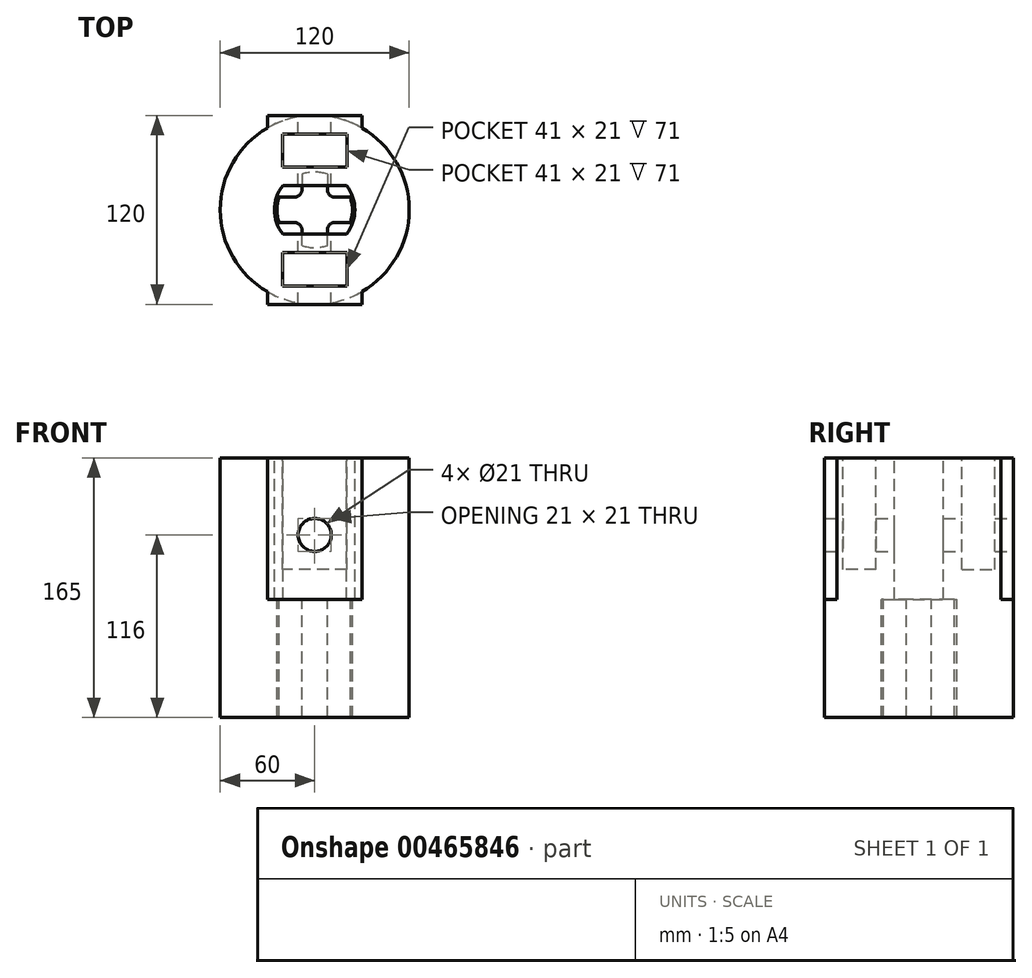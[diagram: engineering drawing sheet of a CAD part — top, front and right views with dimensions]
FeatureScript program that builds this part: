
annotation { "Feature Type Name" : "Feature", "Feature Type Description" : "" }
export const myFeature = defineFeature(function(context is Context, id is Id, definition is map)
    precondition{}
    {
        {
            var Q0;
            Q0=qCreatedBy(makeId("Top.planeOp"),FACE);
            var sketch = newSketch(context, id + "F0", { "sketchPlane" : qUnion([Q0])});
            skCircle(sketch, "E0", {"center": v(0, 0) * mm, "radius": 60 * mm});
            skLineSegment(sketch, "E1", {"start": v(-30, 51.96) * mm, "end": v(-30, 60) * mm});
            skLineSegment(sketch, "E2", {"start": v(-30, 60) * mm, "end": v(30, 60) * mm});
            skLineSegment(sketch, "E3", {"start": v(30, 60) * mm, "end": v(30, 51.96) * mm});
            skLineSegment(sketch, "E4", {"start": v(8, 22.63) * mm, "end": v(8, 13) * mm});
            skArc(sketch, "E5", {"start": v(8, 22.63) * mm, "mid": v(0, 24) * mm, "end": v(-8, 22.63) * mm});
            skArc(sketch, "E6", {"start": v(8, 13) * mm, "mid": v(9.46, 9.46) * mm, "end": v(13, 8) * mm});
            skLineSegment(sketch, "E7", {"start": v(-8, 22.63) * mm, "end": v(0, 0) * mm, "construction": true});
            skLineSegment(sketch, "E8", {"start": v(0, 0) * mm, "end": v(22.63, 8) * mm, "construction": true});
            skLineSegment(sketch, "E9", {"start": v(22.63, 8) * mm, "end": v(13, 8) * mm});
            skLineSegment(sketch, "E10", {"start": v(-8, 22.63) * mm, "end": v(8, 22.63) * mm, "construction": true});
            skArc(sketch, "E11.1.0", {"start": v(-22.63, 8) * mm, "mid": v(-24, 0) * mm, "end": v(-22.63, -8) * mm});
            skLineSegment(sketch, "E11.1.1", {"start": v(-22.63, 8) * mm, "end": v(-13, 8) * mm});
            skArc(sketch, "E11.1.2", {"start": v(-13, 8) * mm, "mid": v(-9.46, 9.46) * mm, "end": v(-8, 13) * mm});
            skLineSegment(sketch, "E11.1.3", {"start": v(-8, 22.63) * mm, "end": v(-8, 13) * mm});
            skArc(sketch, "E11.2.0", {"start": v(-8, -22.63) * mm, "mid": v(0, -24) * mm, "end": v(8, -22.63) * mm});
            skLineSegment(sketch, "E11.2.1", {"start": v(-8, -22.63) * mm, "end": v(-8, -13) * mm});
            skArc(sketch, "E11.2.2", {"start": v(-8, -13) * mm, "mid": v(-9.46, -9.46) * mm, "end": v(-13, -8) * mm});
            skLineSegment(sketch, "E11.2.3", {"start": v(-22.63, -8) * mm, "end": v(-13, -8) * mm});
            skArc(sketch, "E11.3.0", {"start": v(22.63, -8) * mm, "mid": v(24, 0) * mm, "end": v(22.63, 8) * mm});
            skLineSegment(sketch, "E11.3.1", {"start": v(22.63, -8) * mm, "end": v(13, -8) * mm});
            skArc(sketch, "E11.3.2", {"start": v(13, -8) * mm, "mid": v(9.46, -9.46) * mm, "end": v(8, -13) * mm});
            skLineSegment(sketch, "E11.3.3", {"start": v(8, -22.63) * mm, "end": v(8, -13) * mm});
            skLineSegment(sketch, "E12.1.0", {"start": v(-30, -60) * mm, "end": v(-30, -51.96) * mm});
            skLineSegment(sketch, "E12.1.1", {"start": v(30, -60) * mm, "end": v(-30, -60) * mm});
            skLineSegment(sketch, "E12.1.2", {"start": v(30, -51.96) * mm, "end": v(30, -60) * mm});
            skSolve(sketch);
        }
        {
            var Q0;
            Q0=qSketchRegion(id+"F0",true);
            var Q1;
            Q1=makeQuery(id+"F0.imprint","IMPRINT",FACE,{"disambiguationData":[TD([[makeQuery(id+"F0.imprint","IMPRINT",EDGE,{"derivedFrom":sQuery(id+"F0.wireOp",EDGE,"rkZdlgmY-ciTU-kQnJ-2yCQ-PcgXUmxzg4s6")}),-1.0]])]});
            var Q2;
            Q2=makeQuery(id+"F0.imprint","IMPRINT",FACE,{"disambiguationData":[TD([[makeQuery(id+"F0.imprint","IMPRINT",EDGE,{"derivedFrom":sQuery(id+"F0.wireOp",EDGE,"E4")}),-1.0]])]});
            extrude(context, id + "F1", {"entities" : qUnion([Q0, Q1, Q2]), "depth" : 90 * mm, "offsetDistance" : 25 * mm});
        }
        {
            var Q0;
            Q0=makeQuery(id+"F0.imprint","IMPRINT",FACE,{"disambiguationData":[TD([[makeQuery(id+"F0.imprint","IMPRINT",EDGE,{"derivedFrom":sQuery(id+"F0.wireOp",EDGE,"E4")}),1.0]])]});
            extrude(context, id + "F2", {"entities" : qUnion([Q0]), "operationType" : NewBodyOperationType.ADD, "oppositeDirection" : true, "depth" : 75 * mm, "offsetDistance" : 25 * mm});
        }
        {
            var Q0;
            Q0=makeQuery(id+"F1.opExtrude","CAP_FACE",FACE,{"disambiguationData":[OSD([sQuery(id+"F0.wireOp",EDGE,"E0")])],"isStart":false});
            var sketch = newSketch(context, id + "F3", { "sketchPlane" : qUnion([Q0])});
            skLineSegment(sketch, "E13", {"start": v(-20.25, 15.5) * mm, "end": v(20.25, -15.5) * mm, "construction": true});
            skPoint(sketch, "E14", {"position": v(0, 0) * mm});
            skPoint(sketch, "E15", {"position": v(0, 15.5) * mm});
            skCircle(sketch, "E16", {"center": v(0, 0) * mm, "radius": 25.5 * mm});
            skLineSegment(sketch, "E17", {"start": v(-20.25, -15.5) * mm, "end": v(20.25, -15.5) * mm});
            skLineSegment(sketch, "E18", {"start": v(-20.25, 15.5) * mm, "end": v(20.25, 15.5) * mm});
            skSolve(sketch);
        }
        {
            var Q0;
            {var subQ0=sQuery(id+"F3.wireOp",EDGE,"E16");var subQ1=sQuery(id+"F3.wireOp",EDGE,"5hhhO5J8-d6BO-3ee7-2W28-d0MtOCh9Vy86.bottom");var subQ2=makeQuery(id+"F3.imprint","INTERSECT",VERTEX,{"disambiguationData":[OD(0.0)],"derivedFrom":[subQ1,subQ0]});Q0=makeQuery(id+"F3.imprint","IMPRINT",FACE,{"disambiguationData":[TD([[makeQuery(id+"F3.imprint","IMPRINT",EDGE,{"disambiguationData":[TD([[subQ2,-1.0]])],"derivedFrom":subQ1}),-1.0]])]});}
            var Q1;
            {var subQ0=sQuery(id+"F3.wireOp",EDGE,"E17");Q1=makeQuery(id+"F3.imprint","IMPRINT",FACE,{"disambiguationData":[TD([[makeQuery(id+"F3.imprint","IMPRINT",EDGE,{"derivedFrom":subQ0}),1.0]])]});}
            extrude(context, id + "F4", {"entities" : qUnion([Q0, Q1]), "operationType" : NewBodyOperationType.REMOVE, "oppositeDirection" : true, "depth" : 90 * mm, "offsetDistance" : 25 * mm});
        }
        {
            var Q0;
            Q0=makeQuery(id+"F1.opExtrude","SWEPT_FACE",FACE,{"disambiguationData":[OSD([sQuery(id+"F0.wireOp",EDGE,"E2")])]});
            var sketch = newSketch(context, id + "F5", { "sketchPlane" : qUnion([Q0])});
            skSolve(sketch);
        }
        {
            var Q0;
            Q0=makeQuery(id+"F1.opExtrude","CAP_FACE",FACE,{"disambiguationData":[OSD([sQuery(id+"F0.wireOp",EDGE,"E0")])],"isStart":false});
            var sketch = newSketch(context, id + "F6", { "sketchPlane" : qUnion([Q0])});
            skLineSegment(sketch, "E19.bottom", {"start": v(-20.5, 27.25) * mm, "end": v(20.5, 27.25) * mm});
            skLineSegment(sketch, "E19.top", {"start": v(-20.5, 48.25) * mm, "end": v(20.5, 48.25) * mm});
            skLineSegment(sketch, "E19.left", {"start": v(-20.5, 27.25) * mm, "end": v(-20.5, 48.25) * mm});
            skLineSegment(sketch, "E19.right", {"start": v(20.5, 27.25) * mm, "end": v(20.5, 48.25) * mm});
            skLineSegment(sketch, "E20", {"start": v(0, 48.25) * mm, "end": v(0, 60) * mm, "construction": true});
            skLineSegment(sketch, "E21", {"start": v(0, 27.25) * mm, "end": v(0, 15.5) * mm, "construction": true});
            skLineSegment(sketch, "E22.1.0", {"start": v(-20.5, -27.25) * mm, "end": v(-20.5, -48.25) * mm});
            skLineSegment(sketch, "E22.1.1", {"start": v(20.5, -48.25) * mm, "end": v(-20.5, -48.25) * mm});
            skLineSegment(sketch, "E22.1.2", {"start": v(20.5, -27.25) * mm, "end": v(20.5, -48.25) * mm});
            skLineSegment(sketch, "E22.1.3", {"start": v(20.5, -27.25) * mm, "end": v(-20.5, -27.25) * mm});
            skPoint(sketch, "E22.center", {"position": v(0, 0) * mm});
            skSolve(sketch);
        }
        {
            var Q0;
            Q0=qSketchRegion(id+"F6",true);
            extrude(context, id + "F7", {"entities" : qUnion([Q0]), "operationType" : NewBodyOperationType.REMOVE, "oppositeDirection" : true, "depth" : 71 * mm, "offsetDistance" : 25 * mm});
        }
        {
            var Q0;
            {var subQ0=sQuery(id+"F0.wireOp",EDGE,"E2");Q0=makeQuery(id+"F5.imprint","IMPRINT",FACE,{"disambiguationData":[TD([[makeQuery(id+"F5.imprint","IMPRINT",EDGE,{"derivedFrom":makeQuery(id+"F1.opExtrude","CAP_EDGE",EDGE,{"disambiguationData":[OSD([subQ0])],"isStart":true})}),-1.0]])]});}
            var sketch = newSketch(context, id + "F8", { "sketchPlane" : qUnion([Q0])});
            skCircle(sketch, "E23", {"center": v(0, 41) * mm, "radius": 10.5 * mm});
            skSolve(sketch);
        }
        {
            var Q0;
            Q0=makeQuery(id+"F8.imprint","IMPRINT",FACE,{"disambiguationData":[TD([[makeQuery(id+"F8.imprint","IMPRINT",EDGE,{"derivedFrom":sQuery(id+"F8.wireOp",EDGE,"E23")}),1.0]])]});
            extrude(context, id + "F9", {"entities" : qUnion([Q0]), "operationType" : NewBodyOperationType.REMOVE, "oppositeDirection" : true, "depth" : 200 * mm, "offsetDistance" : 25 * mm});
        }
    });
